# Revit family: RBA4115-936
name_source: partatom
category: Plumbing Fixtures
units: mm (PartAtom-declared; Revit-internal decimal feet)

## family parameters
Always vertical = Yes
Cut with Voids When Loaded = No
Part Type = Normal
Room Calculation Point = No
Round Connector Dimension = Use Diameter
Shared = Yes
Work Plane-Based = No

## types (1)
- RBA4115-936
    CW Connection = Yes
    Default Elevation = 0 mm  [stored 0 ft]
    Description = 5 Star Shower T-Rail Kit, RH, Matte Black
    Distance Away from Toilet (default) = 1090 mm  [stored 3.57612 ft]
    Distance Away from Wall (default) = 100 mm  [stored 0.328084 ft]
    HW Connection = Yes
    Manufacturer = RBA Group
    Materials and Finishes = Stainless Steel Matte Black Finish
    Model = RBA4115-936
    OFFSET = 1000 mm  [stored 3.28084 ft]
    URL = www.rba.com.au
    Vent Connection = Yes
    Waste Connection = Yes

note: [stored X ft] marks values corroborated as IEEE doubles in the binary element streams (Revit-internal decimal feet)

## geometry (parser evidence)
native form markers: Blend x4, Sweep x7
no freeform markers — native parametric forms only
